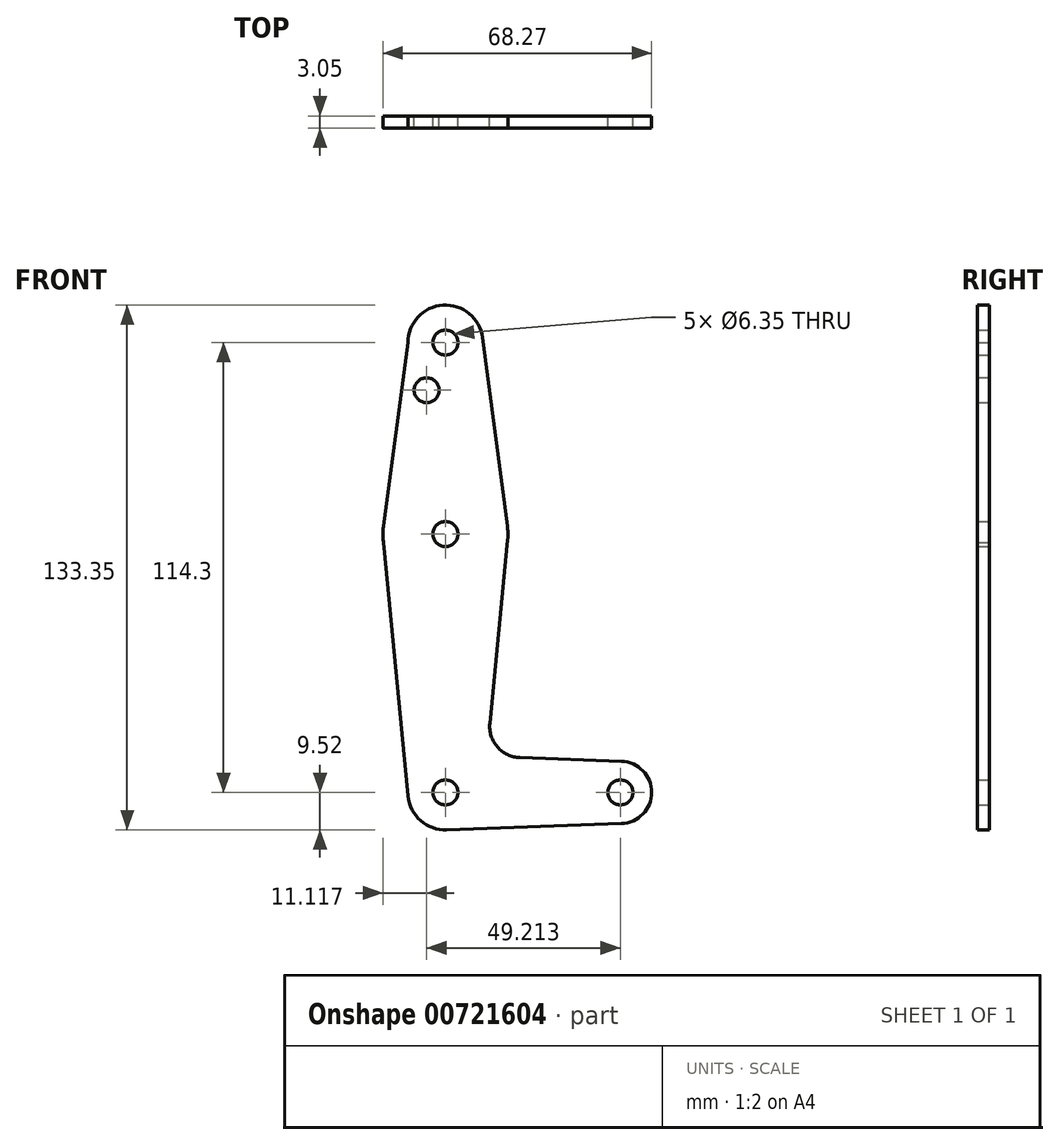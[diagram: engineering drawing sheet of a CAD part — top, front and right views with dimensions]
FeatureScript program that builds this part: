
annotation { "Feature Type Name" : "Feature", "Feature Type Description" : "" }
export const myFeature = defineFeature(function(context is Context, id is Id, definition is map)
    precondition{}
    {
        {
            var Q0;
            Q0=qCreatedBy(makeId("Front.planeOp"),FACE);
            var sketch = newSketch(context, id + "F0", { "sketchPlane" : qUnion([Q0])});
            skLineSegment(sketch, "E0", {"start": v(0, 114.3) * mm, "end": v(0, 0) * mm, "construction": true});
            skLineSegment(sketch, "E1", {"start": v(0, 0) * mm, "end": v(44.45, 0) * mm, "construction": true});
            skCircle(sketch, "E2", {"center": v(0, 114.3) * mm, "radius": 9.53 * mm});
            skCircle(sketch, "E3", {"center": v(0, 0) * mm, "radius": 9.53 * mm});
            skCircle(sketch, "E4", {"center": v(44.45, 0) * mm, "radius": 7.94 * mm});
            skCircle(sketch, "E5", {"center": v(0, 65.65) * mm, "radius": 15.88 * mm});
            skLineSegment(sketch, "E6", {"start": v(-9.53, 114.3) * mm, "end": v(-15.74, 67.75) * mm});
            skLineSegment(sketch, "E7", {"start": v(-15.74, 67.75) * mm, "end": v(-15.74, 63.55) * mm});
            skLineSegment(sketch, "E8", {"start": v(-15.74, 63.55) * mm, "end": v(-9.48, -0.92) * mm});
            skLineSegment(sketch, "E9", {"start": v(0.34, -9.52) * mm, "end": v(44.73, -7.93) * mm});
            skLineSegment(sketch, "E10", {"start": v(45.07, 7.92) * mm, "end": v(18.9, 8.86) * mm});
            skLineSegment(sketch, "E11", {"start": v(15.74, 67.72) * mm, "end": v(9.44, 115.54) * mm});
            skCircle(sketch, "E12", {"center": v(0, 114.3) * mm, "radius": 3.18 * mm});
            skCircle(sketch, "E13", {"center": v(0, 65.65) * mm, "radius": 3.18 * mm});
            skCircle(sketch, "E14", {"center": v(0, 0) * mm, "radius": 3.18 * mm});
            skCircle(sketch, "E15", {"center": v(44.45, 0) * mm, "radius": 3.18 * mm});
            skLineSegment(sketch, "E16", {"start": v(15.8, 64.12) * mm, "end": v(11.28, 17.57) * mm});
            skCircle(sketch, "E17", {"center": v(-4.76, 102.18) * mm, "radius": 3.18 * mm});
            skArc(sketch, "E18.filletArc", {"start": v(11.28, 17.57) * mm, "mid": v(13.2, 11.56) * mm, "end": v(18.9, 8.86) * mm});
            skSolve(sketch);
        }
        {
            var Q0;
            Q0 = qSketchRegion(id + "F0", true);
            extrude(context, id + "F1", {"entities" : qUnion([Q0]), "depth" : 3.05 * mm, "offsetDistance" : 25.4 * mm});
        }
    });
